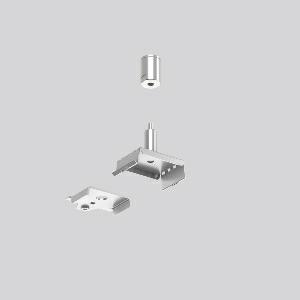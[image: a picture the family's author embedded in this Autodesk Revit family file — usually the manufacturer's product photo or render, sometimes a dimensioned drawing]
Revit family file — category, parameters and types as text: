
# Revit family: linedo_pendelset_ohne_seil_982663_000_f412
name_source: partatom
category: Lighting Fixtures
units: mm (PartAtom-declared; Revit-internal decimal feet)

## family parameters
Cut with Voids When Loaded = No
Host = Face
Light Source = No
Part Type = Normal
Room Calculation Point = No
Round Connector Dimension = Use Diameter
Shared = No

## types (1)
- LINEDO Pendelset ohne Seil
    Apparent Load = 0 VA
    Default Elevation = 1800 mm
    Description = Suspension for steel cable (cable not included). Spring steel, blank, for installing continuous line luminaire modules.
Colour: unpainted
Length: 33 mm
Width: 54 mm
Weight: 60 g
Type of Installation: pendant
    Height = 0 mm  [stored 0 ft]
    Lamp = 0 x
    Length = 33 mm
    Luminous efficacy = 0 lm/W
    Manufacturer = RZB
    ModVariant = No
    Model = 982663.000
    Mounting Place = Ceiling
    Mounting Type = Surface mounted
    Number of Poles = 1
    OnlyDefault = Yes
    Power Factor = 1
    Product Name = LINEDO Pendelset ohne Seil
    Product group = Surface mounted continuous line luminaire system
    ProductGroupID = 310
    Protection Class = Protection class
    Protection Degree = Degree of protection
    RLX_Detail_Level = 1
    RLX_Emergency_Light_Flux = 0 lm
    RLX_Emergency_Type = 0
    RLX_Emergency_Type_DB = No
    RlxData = <blob elided: 15189 chars, md5=dae8f74b>
    Standby Power = 0 W
    System Light Flux = 0 lm
    System Power = 0 W
    Type Comments = Product without accessories
    Type Image = 982663.000.jpg
    URL = http://relux.com
    VarID = ---
    Voltage = 0 V
    Weight = 0.00 kg
    Width = 54 mm

note: [stored X ft] marks values corroborated as IEEE doubles in the binary element streams (Revit-internal decimal feet)

## geometry (parser evidence)
native form markers: Sweep x11
no freeform markers — native parametric forms only
